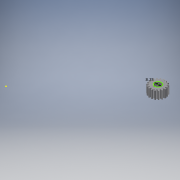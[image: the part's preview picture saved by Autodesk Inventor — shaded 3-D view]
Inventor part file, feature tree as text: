
AUTODESK INVENTOR PART (.ipt)
format: ipt  version: 2019 (Build 230136000, 136)  size: 970,240 bytes
history: native  units: mm (DEFAULTED — no unit token found)
features: extrude x3, fillet x3, chamfer x2, sketch x1
ambient origin geometry x8: Origin, YZ Plane, XZ Plane, XY Plane, X Axis, Y Axis, Z Axis, Center Point
bodies: Solid1 (feature_tree)
feature tree (9):
  extrude  "Kihúzás2"  Depth=10.0mm
  fillet  "Lekerekítés1"  Radius=0.4mm
  fillet  "Lekerekítés2"  Radius=8.0mm
  extrude  "Kihúzás3"  Depth=10.0mm TaperAngle=0.0deg
  chamfer  "Letörés1"  Distance=0.4mm Angle=45.0deg
  extrude  "Kihúzás4"  Depth=10.0mm
  fillet  "Lekerekítés3"  Radius=1.0mm
  chamfer  "Letörés2"  Distance=4.9mm
  sketch  "Sketch4"  dims[d2=10.0mm d3=0.0mm d4=0.4mm d5=0.4mm d6=8.0mm d7=10.0mm d8=0.0mm d9=0.4mm d10=2.0mm d11=45.0deg d12=2.0mm d13=1.0mm d14=4.9mm d15=10.0mm d16=0.0mm d17=0.1mm d18=0.1mm d19=2.0mm d20=45.0deg d21=8.35mm]
